# Revit family: BR-BA
name_source: partatom
category: Устройства связи
revit_build: Autodesk Revit 2016 (Build: 20160314_0715(x64)
units: mm (PartAtom-declared; Revit-internal decimal feet)

## family parameters
Всегда вертикально = Нет
На основе рабочей плоскости = Да
Общий = Да
При загрузке вырезать с полостями = Нет
Размер круглого соединителя = Использовать диаметр
Сохранять ориентацию аннотаций = Нет
Тип детали = Нормальный
Точка расчета площади = Нет

## types (1)
- BR-BA
    ADSK_URL страницы изделия = https://www.bas-ip.ru
    ADSK_Версия Revit = Revit 2016
    ADSK_Единица измерения = шт
    ADSK_Завод-изготовитель = BAS-IP
    ADSK_Марка = BR-BA
    ADSK_Наименование = КРОНШТЕЙН BR-BA
    ADSK_Наименование краткое = BR-BA
    ADSK_Размер_Длина = 104 мм
    ADSK_Размер_Толщина = 61 мм
    ADSK_Размер_Ширина = 276 мм
    BIM library = https://bimlib.ru
    URL = https://www.bas-ip.ru
    Группа модели = Кронштейн
    Изготовитель = BAS-IP
    Изображение типоразмера = <Нет>
    Материал корпуса = SHV_Краска Черная
    Описание = Кронштейн с козырьком для накладного монтажа панелей BA-04 и BA-08.
    Отметка по умолчанию = 0 мм
    Размер = 276х104х61 мм
    Цвет = Черный
